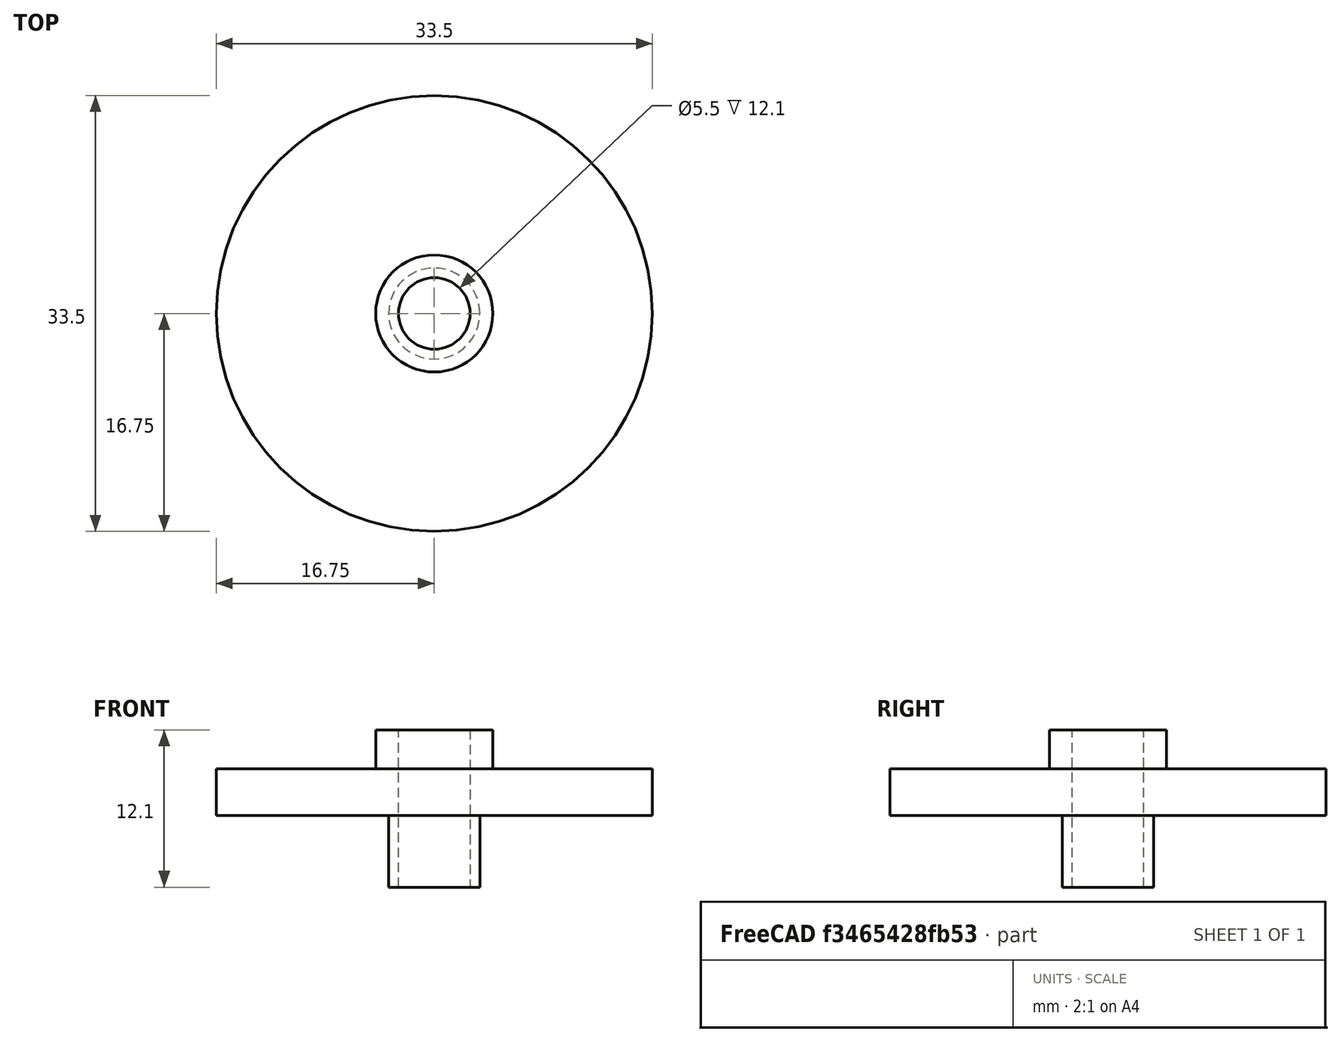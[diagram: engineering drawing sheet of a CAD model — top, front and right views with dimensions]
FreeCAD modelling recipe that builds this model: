
FCSTD DOCUMENT  (FreeCAD 0.18R16110 (Git))
Label: gear_5.5x33.5
License: All rights reserved
LicenseURL: http://en.wikipedia.org/wiki/All_rights_reserved
objects: Sketcher::SketchObject×4, PartDesign::Pad×3, PartDesign::Body×1, PartDesign::Pocket×1
note: 13 computed .brp shape members not serialized (recipe doc carries the construction recipe); baked Part::Feature solids carry a one-line shape summary decoded from their .brp

FEATURE [Sketcher::SketchObject] Sketch
  MapMode = 5
  Support = -> [XY_Plane]
  sketch-geometry (1):
    g0: Circle CenterX=0 CenterY=0 CenterZ=0 NormalX=0 NormalY=0 NormalZ=1 AngleXU=0 Radius=16.75
  constraints (2):
    c: Coincident(g0,g-1)
    c: Diameter(g0) = 33.5
FEATURE [PartDesign::Pad] Pad
  Length = 3.6
  Length2 = 100
  Profile = -> Sketch
  Type = 0
FEATURE [Sketcher::SketchObject] Sketch001
  MapMode = 5
  Placement = pos=(0,0,3.6) rot=(0,0,1;0rad)
  Support = -> [Pad]
  sketch-geometry (1):
    g0: Circle CenterX=0 CenterY=0 CenterZ=0 NormalX=0 NormalY=0 NormalZ=1 AngleXU=0 Radius=4.5
  constraints (2):
    c: Coincident(g0,g-1)
    c: Diameter(g0) = 9
FEATURE [PartDesign::Body] Body
  Group = -> [Sketch,Pad,Sketch001,Sketch002,Sketch003,Pad002,Pad001,Pocket]
  Origin = -> Origin
  Tip = -> Pocket
FEATURE [PartDesign::Pad] Pad001
  BaseFeature = -> Pad002
  Length = 3
  Length2 = 100
  Profile = -> Sketch001
  Type = 0
FEATURE [Sketcher::SketchObject] Sketch002
  MapMode = 5
  Placement = pos=(0,0,6.6) rot=(0,0,1;0rad)
  Support = -> [Pad001]
  sketch-geometry (1):
    g0: Circle CenterX=0 CenterY=0 CenterZ=0 NormalX=0 NormalY=0 NormalZ=1 AngleXU=0 Radius=2.75
  constraints (2):
    c: Coincident(g-1,g0)
    c: Diameter(g0) = 5.5
FEATURE [PartDesign::Pocket] Pocket
  BaseFeature = -> Pad001
  Length = 5
  Length2 = 100
  Profile = -> Sketch002
  Type = 1
FEATURE [Sketcher::SketchObject] Sketch003
  MapMode = 5
  Placement = pos=(0,0,0) rot=(1,0,0;3.14159rad)
  Support = -> [Pocket]
  sketch-geometry (1):
    g0: Circle CenterX=0 CenterY=0 CenterZ=0 NormalX=0 NormalY=0 NormalZ=1 AngleXU=0 Radius=3.5
  constraints (2):
    c: Coincident(g0,g-1)
    c: Diameter(g0) = 7
FEATURE [PartDesign::Pad] Pad002
  BaseFeature = -> Pad
  Length = 5.5
  Length2 = 100
  Profile = -> Sketch003
  Type = 0
